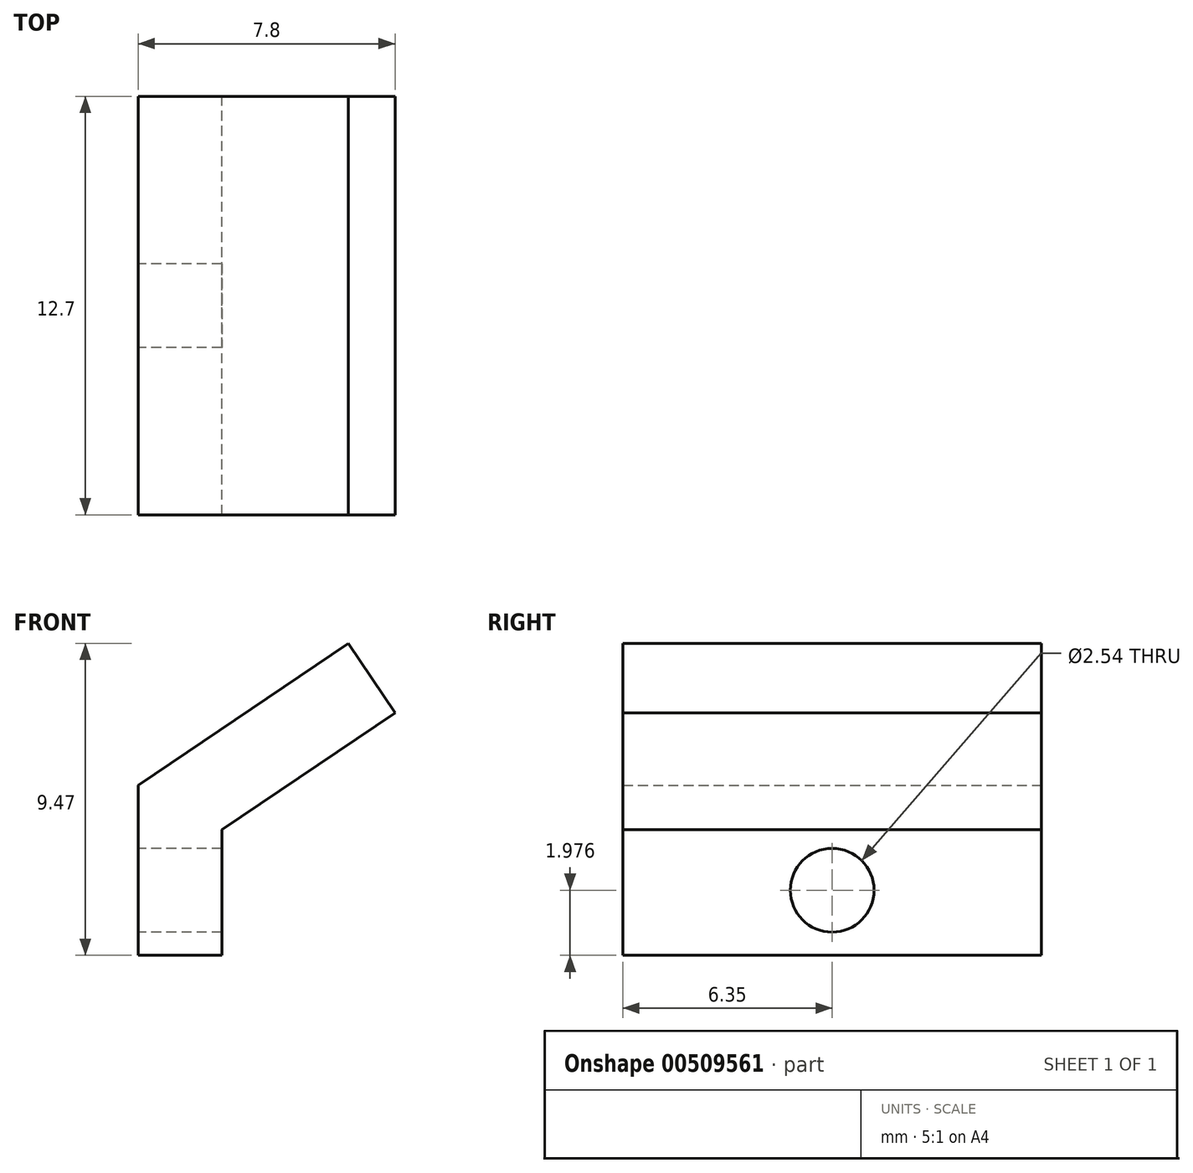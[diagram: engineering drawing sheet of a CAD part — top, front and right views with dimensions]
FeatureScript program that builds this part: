
annotation { "Feature Type Name" : "Feature", "Feature Type Description" : "" }
export const myFeature = defineFeature(function(context is Context, id is Id, definition is map)
    precondition{}
    {
        {
            var Q0;
            Q0=qCreatedBy(makeId("Front.planeOp"),FACE);
            var sketch = newSketch(context, id + "F0", { "sketchPlane" : qUnion([Q0])});
            skLineSegment(sketch, "E0", {"start": v(0, 0) * mm, "end": v(-2.54, 0) * mm});
            skLineSegment(sketch, "E1", {"start": v(-2.54, 0) * mm, "end": v(-2.54, 6.35) * mm});
            skLineSegment(sketch, "E2", {"start": v(0, 0) * mm, "end": v(0, 3.81) * mm});
            skLineSegment(sketch, "E3", {"start": v(0, 3.81) * mm, "end": v(5.26, 7.36) * mm});
            skLineSegment(sketch, "E4", {"start": v(5.26, 7.36) * mm, "end": v(3.84, 9.47) * mm});
            skLineSegment(sketch, "E5", {"start": v(3.84, 9.47) * mm, "end": v(-2.54, 5.16) * mm});
            skSolve(sketch);
        }
        {
            var Q0;
            {var subQ1=sQuery(id+"F0.wireOp",EDGE,"E0");Q0=makeQuery(id+"F0.imprint","IMPRINT",FACE,{"disambiguationData":[TD([[makeQuery(id+"F0.imprint","IMPRINT",EDGE,{"derivedFrom":subQ1}),-1.0]])]});}
            extrude(context, id + "F1", {"entities" : qUnion([Q0]), "depth" : 12.7 * mm});
        }
        {
            var Q0;
            Q0=makeQuery(id+"F1.opExtrude","SWEPT_FACE",FACE,{"disambiguationData":[OSD([sQuery(id+"F0.wireOp",EDGE,"E1")])]});
            var sketch = newSketch(context, id + "F2", { "sketchPlane" : qUnion([Q0])});
            skCircle(sketch, "E6", {"center": v(6.35, 1.98) * mm, "radius": 1.27 * mm});
            skPoint(sketch, "E6.centerSnap0", {"position": v(6.35, 0) * mm});
            skSolve(sketch);
        }
        {
            var Q0;
            Q0=makeQuery(id+"F2.imprint","IMPRINT",FACE,{"disambiguationData":[TD([[makeQuery(id+"F2.imprint","IMPRINT",EDGE,{"derivedFrom":sQuery(id+"F2.wireOp",EDGE,"E6")}),1.0]])]});
            extrude(context, id + "F3", {"entities" : qUnion([Q0]), "operationType" : NewBodyOperationType.REMOVE, "oppositeDirection" : true, "depth" : 25.4 * mm});
        }
    });
